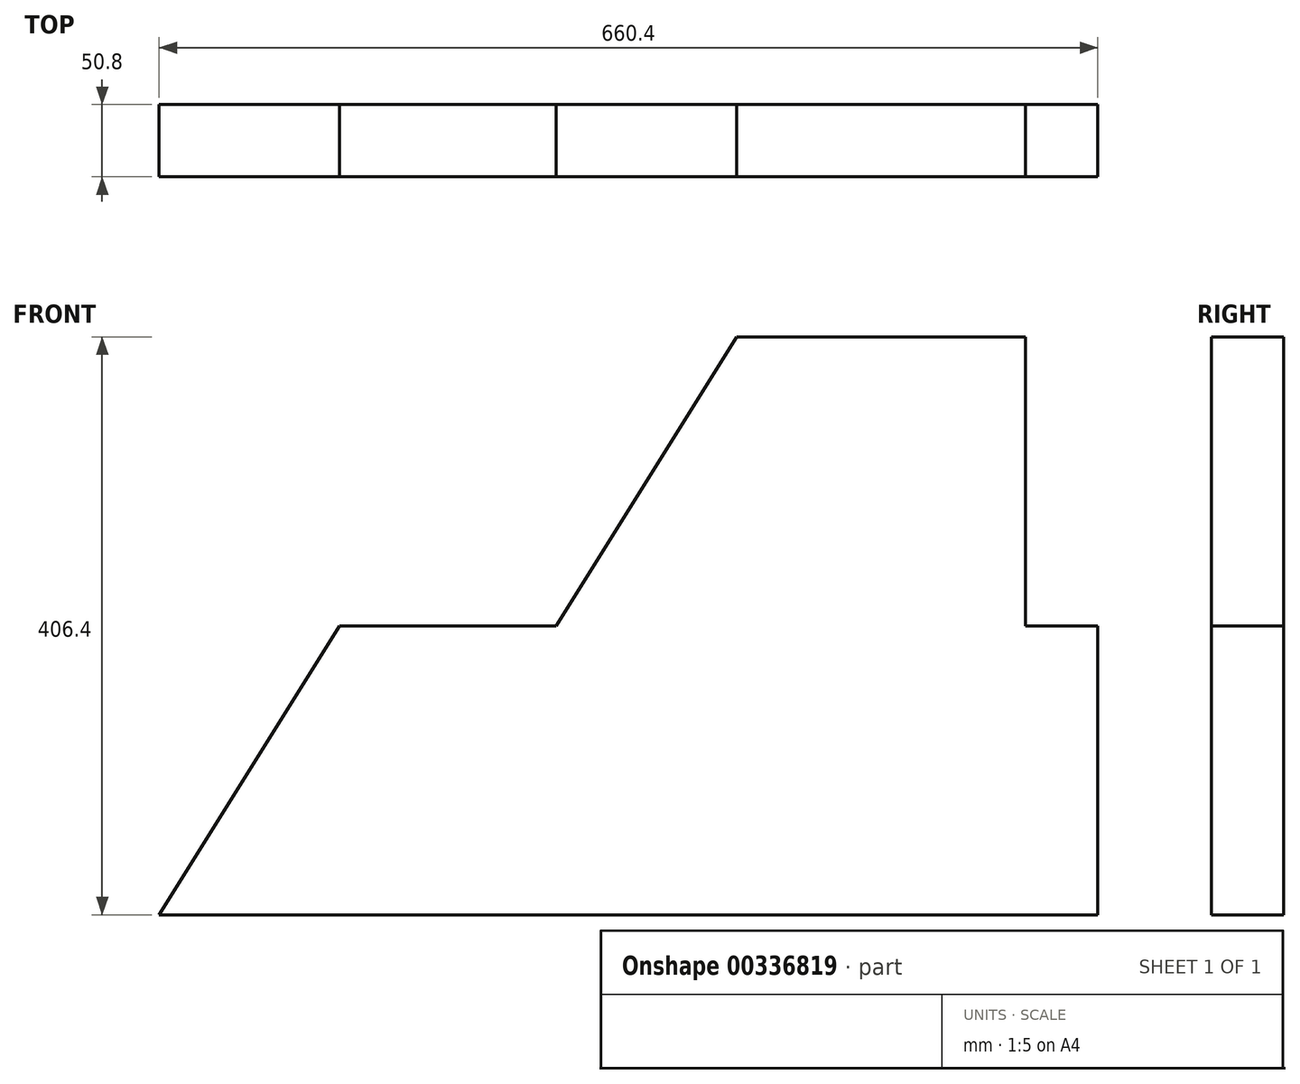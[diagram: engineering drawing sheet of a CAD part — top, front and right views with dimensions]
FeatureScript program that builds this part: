
annotation { "Feature Type Name" : "Feature", "Feature Type Description" : "" }
export const myFeature = defineFeature(function(context is Context, id is Id, definition is map)
    precondition{}
    {
        {
            var Q0;
            Q0=qCreatedBy(makeId("Front.planeOp"),FACE);
            var sketch = newSketch(context, id + "F0", { "sketchPlane" : qUnion([Q0])});
            skLineSegment(sketch, "E0", {"start": v(115.55, 286.25) * mm, "end": v(318.75, 286.25) * mm});
            skLineSegment(sketch, "E1", {"start": v(318.75, 286.25) * mm, "end": v(318.75, 83.05) * mm});
            skLineSegment(sketch, "E2", {"start": v(318.75, 83.05) * mm, "end": v(369.55, 83.05) * mm});
            skLineSegment(sketch, "E3", {"start": v(369.55, 83.05) * mm, "end": v(369.55, -120.15) * mm});
            skLineSegment(sketch, "E4", {"start": v(369.55, -120.15) * mm, "end": v(-290.85, -120.15) * mm});
            skLineSegment(sketch, "E5", {"start": v(-290.85, -120.15) * mm, "end": v(-163.85, 83.05) * mm});
            skLineSegment(sketch, "E6", {"start": v(-163.85, 83.05) * mm, "end": v(-11.45, 83.05) * mm});
            skLineSegment(sketch, "E7", {"start": v(-11.45, 83.05) * mm, "end": v(115.55, 286.25) * mm});
            skSolve(sketch);
        }
        {
            var Q0;
            Q0=makeQuery(id+"F0.imprint","IMPRINT",FACE,{"disambiguationData":[TD([[makeQuery(id+"F0.imprint","IMPRINT",EDGE,{"derivedFrom":sQuery(id+"F0.wireOp",EDGE,"E0")}),-1.0]])]});
            extrude(context, id + "F1", {"entities" : qUnion([Q0]), "depth" : 50.8 * mm});
        }
    });
